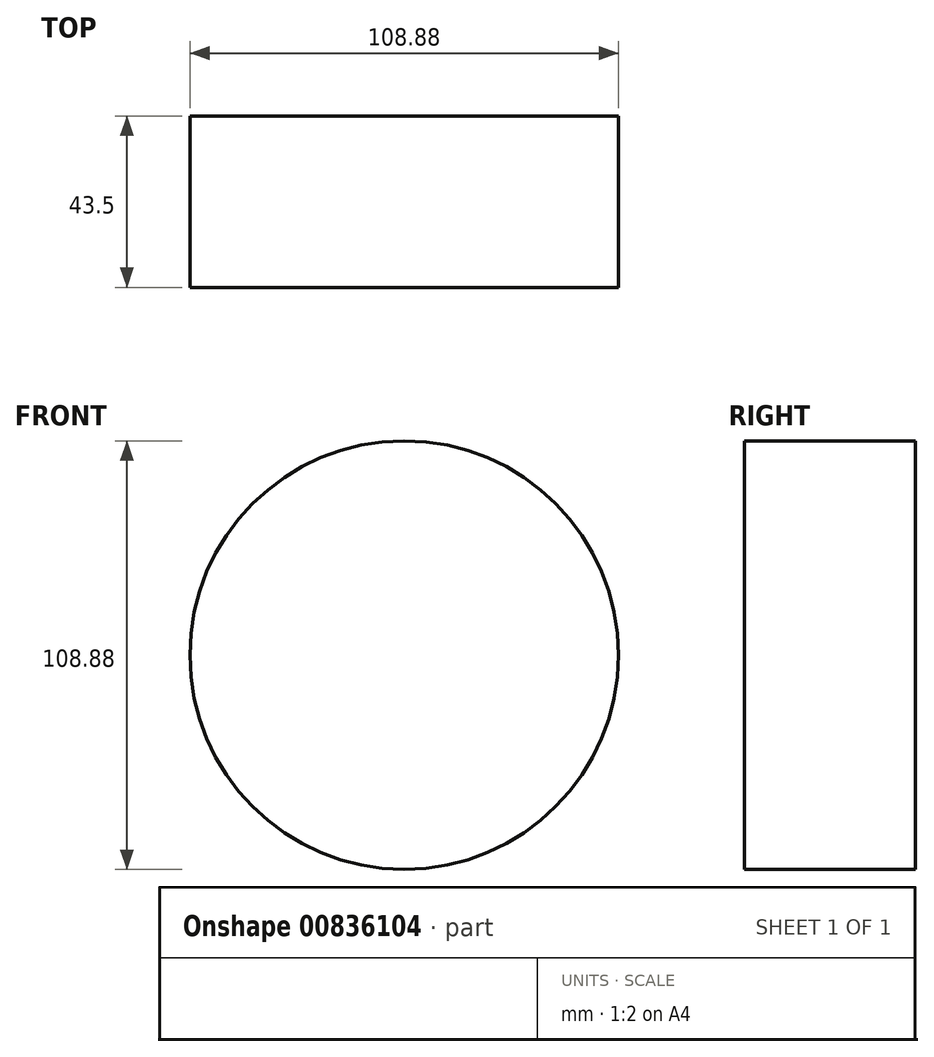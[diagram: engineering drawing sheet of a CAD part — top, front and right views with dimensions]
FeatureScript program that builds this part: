
annotation { "Feature Type Name" : "Feature", "Feature Type Description" : "" }
export const myFeature = defineFeature(function(context is Context, id is Id, definition is map)
    precondition{}
    {
        {
            var Q0;
            Q0=qCreatedBy(makeId("Front.planeOp"),FACE);
            var sketch = newSketch(context, id + "F0", { "sketchPlane" : qUnion([Q0])});
            skCircle(sketch, "E0", {"center": v(0, -102.78) * mm, "radius": 54.44 * mm});
            skSolve(sketch);
        }
        {
            var Q0;
            Q0=sQuery(id+"F0.wireOp",EDGE,"E0");
            extrude(context, id + "F1", {"bodyType" : ToolBodyType.SURFACE, "surfaceEntities" : qUnion([Q0]), "depth" : 43.5 * mm, "offsetDistance" : 25.4 * mm});
        }
    });
